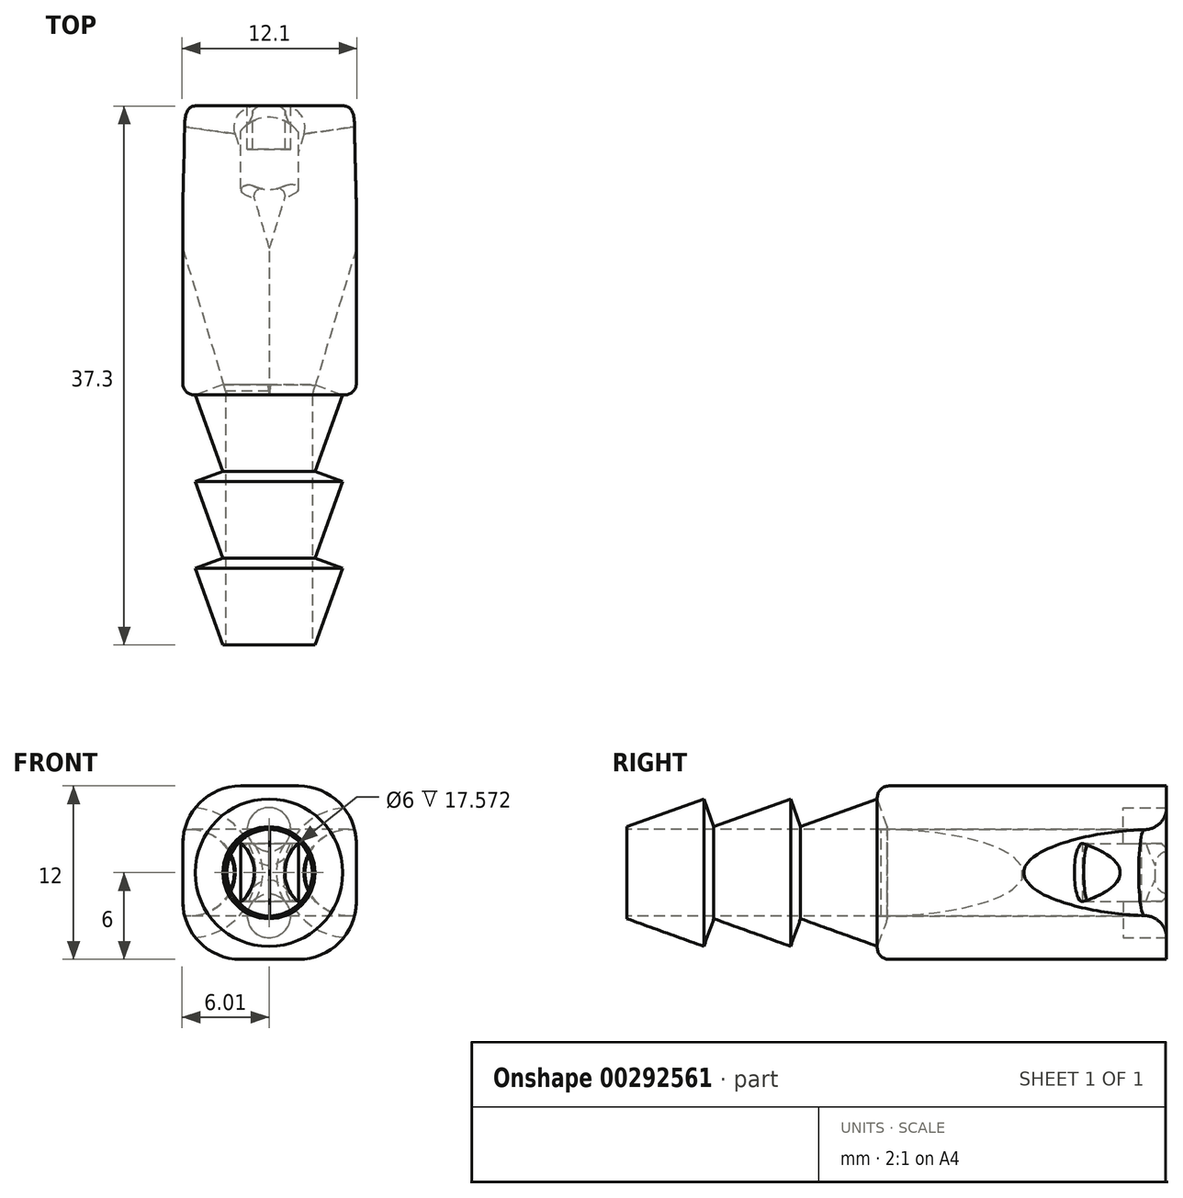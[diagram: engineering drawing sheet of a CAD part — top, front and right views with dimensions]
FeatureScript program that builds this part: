
annotation { "Feature Type Name" : "Feature", "Feature Type Description" : "" }
export const myFeature = defineFeature(function(context is Context, id is Id, definition is map)
    precondition{}
    {
        {
            var Q0;
            Q0=qCreatedBy(makeId("Right.planeOp"),FACE);
            var sketch = newSketch(context, id + "F0", { "sketchPlane" : qUnion([Q0])});
            skLineSegment(sketch, "E0", {"start": v(-28.57, 3.19) * mm, "end": v(-23.26, 5.1) * mm});
            skLineSegment(sketch, "E1", {"start": v(-23.26, 5.1) * mm, "end": v(-22.57, 3.19) * mm});
            skLineSegment(sketch, "E2", {"start": v(-22.57, 3.19) * mm, "end": v(-17.26, 5.1) * mm});
            skLineSegment(sketch, "E3", {"start": v(-17.26, 5.1) * mm, "end": v(-16.57, 3.19) * mm});
            skLineSegment(sketch, "E4", {"start": v(-16.57, 3.19) * mm, "end": v(-11.26, 5.1) * mm});
            skLineSegment(sketch, "E5", {"start": v(-11.26, 5.1) * mm, "end": v(-10.57, 3.19) * mm});
            skLineSegment(sketch, "E6", {"start": v(-10.57, 3.19) * mm, "end": v(-10.57, 0) * mm});
            skLineSegment(sketch, "E7", {"start": v(-28.57, 3.19) * mm, "end": v(-28.57, 0) * mm});
            skLineSegment(sketch, "E8", {"start": v(-28.57, 0) * mm, "end": v(-10.57, 0) * mm});
            skSolve(sketch);
        }
        {
            var Q0;
            Q0 = qSketchRegion(id + "F0", true);
            var Q1;
            Q1=sQuery(id+"F0.wireOp",EDGE,"E8");
            revolve(context, id + "F1", {"entities" : qUnion([Q0]), "axis" : qUnion([Q1]), "revolveType" : RevolveType.FULL});
        }
        {
            var Q0;
            Q0=makeQuery(id+"F1.opRevolve","SWEPT_FACE",FACE,{"disambiguationData":[OSD([sQuery(id+"F0.wireOp",EDGE,"E7")])]});
            var sketch = newSketch(context, id + "F2", { "sketchPlane" : qUnion([Q0])});
            skCircle(sketch, "E9", {"center": v(0, 0) * mm, "radius": 3 * mm});
            skSolve(sketch);
        }
        {
            var Q0;
            Q0=makeQuery(id+"F2.imprint","IMPRINT",FACE,{"disambiguationData":[TD([[makeQuery(id+"F2.imprint","IMPRINT",EDGE,{"derivedFrom":sQuery(id+"F2.wireOp",EDGE,"E9")}),1.0]])]});
            extrude(context, id + "F3", {"entities" : qUnion([Q0]), "operationType" : NewBodyOperationType.REMOVE, "oppositeDirection" : true, "depth" : 18.3 * mm});
        }
        {
            var Q0;
            Q0=qCreatedBy(makeId("Top.planeOp"),FACE);
            var sketch = newSketch(context, id + "F4", { "sketchPlane" : qUnion([Q0])});
            skLineSegment(sketch, "E10.bottom", {"start": v(-5.96, -11.27) * mm, "end": v(6.04, -11.27) * mm});
            skLineSegment(sketch, "E10.top", {"start": v(-5.96, 8.73) * mm, "end": v(6.04, 8.73) * mm});
            skLineSegment(sketch, "E10.left", {"start": v(-5.96, -11.27) * mm, "end": v(-5.96, 8.73) * mm});
            skLineSegment(sketch, "E10.right", {"start": v(6.04, -11.27) * mm, "end": v(6.04, 8.73) * mm});
            skSolve(sketch);
        }
        {
            var Q0;
            Q0 = qSketchRegion(id + "F4", true);
            extrude(context, id + "F5", {"entities" : qUnion([Q0]), "depth" : 6 * mm, "hasSecondDirection" : true, "secondDirectionOppositeDirection" : true, "secondDirectionDepth" : 6 * mm});
        }
        {
            var Q0;
            Q0=makeQuery(id+"F5.opExtrude","CAP_FACE",FACE,{"disambiguationData":[OSD([sQuery(id+"F4.wireOp",EDGE,"E10.bottom"),sQuery(id+"F4.wireOp",EDGE,"E10.top"),sQuery(id+"F4.wireOp",EDGE,"E10.left"),sQuery(id+"F4.wireOp",EDGE,"E10.right")])],"isStart":false});
            var sketch = newSketch(context, id + "F6", { "sketchPlane" : qUnion([Q0])});
            skLineSegment(sketch, "E11", {"start": v(6.04, 8.73) * mm, "end": v(0.04, -11.27) * mm});
            skLineSegment(sketch, "E12", {"start": v(6.04, 8.73) * mm, "end": v(16.48, 27.61) * mm});
            skLineSegment(sketch, "E13", {"start": v(16.48, 27.61) * mm, "end": v(-16.93, 27.61) * mm});
            skLineSegment(sketch, "E14", {"start": v(-16.93, 27.61) * mm, "end": v(-5.96, 8.73) * mm});
            skLineSegment(sketch, "E15", {"start": v(-5.96, 8.73) * mm, "end": v(0.04, -11.27) * mm});
            skSolve(sketch);
        }
        {
            var Q0;
            Q0=makeQuery(id+"F5.opExtrude","SWEPT_FACE",FACE,{"disambiguationData":[OSD([sQuery(id+"F4.wireOp",EDGE,"E10.bottom")])]});
            var sketch = newSketch(context, id + "F7", { "sketchPlane" : qUnion([Q0])});
            skCircle(sketch, "E16", {"center": v(0, 0) * mm, "radius": 3 * mm});
            skSolve(sketch);
        }
        {
            var Q0;
            Q0=makeQuery(id+"F7.imprint","IMPRINT",FACE,{"disambiguationData":[TD([[makeQuery(id+"F7.imprint","IMPRINT",EDGE,{"derivedFrom":sQuery(id+"F7.wireOp",EDGE,"E16")}),1.0]])]});
            var Q1;
            Q1=sQuery(id+"F6.wireOp",EDGE,"E11");
            var Q2;
            Q2=sQuery(id+"F6.wireOp",EDGE,"E12");
            var Q3;
            Q3=sQuery(id+"F6.wireOp",EDGE,"E13");
            var Q4;
            Q4=sQuery(id+"F6.wireOp",EDGE,"E14");
            var Q5;
            Q5=sQuery(id+"F6.wireOp",EDGE,"E15");
            sweep(context, id + "F8", {"operationType" : NewBodyOperationType.REMOVE, "profiles" : qUnion([Q0]), "path" : qUnion([Q1, Q2, Q3, Q4, Q5])});
        }
        {
            var Q0;
            Q0=makeQuery(id+"F5.opExtrude","CAP_EDGE",EDGE,{"disambiguationData":[OSD([sQuery(id+"F4.wireOp",EDGE,"E10.left")])],"isStart":true});
            var Q1;
            Q1=makeQuery(id+"F5.opExtrude","CAP_EDGE",EDGE,{"disambiguationData":[OSD([sQuery(id+"F4.wireOp",EDGE,"E10.left")])],"isStart":false});
            var Q2;
            Q2=makeQuery(id+"F5.opExtrude","CAP_EDGE",EDGE,{"disambiguationData":[OSD([sQuery(id+"F4.wireOp",EDGE,"E10.right")])],"isStart":false});
            var Q3;
            Q3=makeQuery(id+"F5.opExtrude","CAP_EDGE",EDGE,{"disambiguationData":[OSD([sQuery(id+"F4.wireOp",EDGE,"E10.right")])],"isStart":true});
            fillet(context, id + "F9", {"entities" : qUnion([Q0, Q1, Q2, Q3]), "radius" : 4 * mm, "tangentPropagation" : true, "allowEdgeOverflow" : false});
        }
        {
            var Q0;
            Q0=makeQuery(id+"F8.boolean.opBoolean","INTERSECT",EDGE,{"derivedFrom":[makeQuery(id+"F5.opExtrude","SWEPT_FACE",FACE,{"disambiguationData":[OSD([sQuery(id+"F4.wireOp",EDGE,"E10.top")])]}),makeQuery(id+"F8.opSweep","SWEPT_FACE",FACE,{"disambiguationData":[OSD([sQuery(id+"F6.wireOp",EDGE,"E15"),sQuery(id+"F7.wireOp",EDGE,"E16")])]})]});
            var Q1;
            Q1=makeQuery(id+"F8.boolean.opBoolean","INTERSECT",EDGE,{"derivedFrom":[makeQuery(id+"F5.opExtrude","SWEPT_FACE",FACE,{"disambiguationData":[OSD([sQuery(id+"F4.wireOp",EDGE,"E10.top")])]}),makeQuery(id+"F8.opSweep","SWEPT_FACE",FACE,{"disambiguationData":[OSD([sQuery(id+"F6.wireOp",EDGE,"E11"),sQuery(id+"F7.wireOp",EDGE,"E16")])]})]});
            fillet(context, id + "F10", {"entities" : qUnion([Q0, Q1]), "radius" : 1.5 * mm, "tangentPropagation" : true, "allowEdgeOverflow" : false});
        }
        {
            var Q0;
            Q0=makeQuery(id+"F9.opFillet","BLEND_EDGE",EDGE,{"blendedFrom":[makeQuery(id+"F5.opExtrude","CAP_EDGE",EDGE,{"disambiguationData":[OSD([sQuery(id+"F4.wireOp",EDGE,"E10.left")])],"isStart":false}),makeQuery(id+"F5.opExtrude","SWEPT_FACE",FACE,{"disambiguationData":[OSD([sQuery(id+"F4.wireOp",EDGE,"E10.bottom")])]})],"blendedInto":[makeQuery(id+"F5.opExtrude","SWEPT_FACE",FACE,{"disambiguationData":[OSD([sQuery(id+"F4.wireOp",EDGE,"E10.bottom")])]})]});
            fillet(context, id + "F11", {"entities" : qUnion([Q0]), "radius" : .8 * mm, "tangentPropagation" : true, "allowEdgeOverflow" : false});
        }
        {
            var Q0;
            Q0=makeQuery(id+"F5.opExtrude","CAP_FACE",FACE,{"disambiguationData":[OSD([sQuery(id+"F4.wireOp",EDGE,"E10.bottom"),sQuery(id+"F4.wireOp",EDGE,"E10.top"),sQuery(id+"F4.wireOp",EDGE,"E10.left"),sQuery(id+"F4.wireOp",EDGE,"E10.right")])],"isStart":false});
            var sketch = newSketch(context, id + "F12", { "sketchPlane" : qUnion([Q0])});
            skCircle(sketch, "E17", {"center": v(0, 5.45) * mm, "radius": 2.5 * mm});
            skSolve(sketch);
        }
        {
            var Q0;
            Q0=makeQuery(id+"F12.imprint","IMPRINT",FACE,{"disambiguationData":[TD([[makeQuery(id+"F12.imprint","IMPRINT",EDGE,{"derivedFrom":sQuery(id+"F12.wireOp",EDGE,"E17")}),1.0]])]});
            extrude(context, id + "F13", {"entities" : qUnion([Q0]), "operationType" : NewBodyOperationType.REMOVE, "oppositeDirection" : true, "depth" : 8 * mm, "hasSecondDirection" : true, "secondDirectionOppositeDirection" : true, "secondDirectionDepth" : 4 * mm});
        }
        {
            var Q0;
            {var subQ0=sQuery(id+"F12.wireOp",EDGE,"E17");var subQ1=sQuery(id+"F4.wireOp",EDGE,"E10.right");var subQ2=sQuery(id+"F4.wireOp",EDGE,"E10.left");var subQ3=makeQuery(id+"F5.opExtrude","CAP_FACE",FACE,{"disambiguationData":[OSD([sQuery(id+"F4.wireOp",EDGE,"E10.bottom"),sQuery(id+"F4.wireOp",EDGE,"E10.top"),subQ2,subQ1])],"isStart":false});Q0=makeQuery(id+"F13.boolean.opBoolean","INTERSECT",EDGE,{"derivedFrom":[makeQuery(id+"F8.boolean.opBoolean","COPY",FACE,{"derivedFrom":makeQuery(id+"F8.opSweep","SWEPT_FACE",FACE,{"disambiguationData":[OSD([sQuery(id+"F6.wireOp",EDGE,"E11"),sQuery(id+"F7.wireOp",EDGE,"E16")])]})}),makeQuery(id+"F13.opExtrude","SWEPT_FACE",FACE,{"disambiguationData":[OSD([subQ0]),TDD([makeQuery(id+"F12.imprint","IMPRINT",EDGE,{"disambiguationData":[TD([[makeQuery(id+"F12.imprint","INTERSECT",VERTEX,{"disambiguationData":[OD(1.0)],"derivedFrom":[makeQuery(id+"F9.opFillet","BLEND_EDGE",EDGE,{"blendedFrom":[makeQuery(id+"F5.opExtrude","CAP_EDGE",EDGE,{"disambiguationData":[OSD([subQ2])],"isStart":false}),subQ3],"blendedInto":[subQ3]}),subQ0]}),-1.0]])],"derivedFrom":subQ0})])]})]});}
            var Q1;
            {var subQ0=sQuery(id+"F12.wireOp",EDGE,"E17");var subQ1=sQuery(id+"F4.wireOp",EDGE,"E10.right");var subQ2=sQuery(id+"F4.wireOp",EDGE,"E10.left");var subQ3=makeQuery(id+"F5.opExtrude","CAP_FACE",FACE,{"disambiguationData":[OSD([sQuery(id+"F4.wireOp",EDGE,"E10.bottom"),sQuery(id+"F4.wireOp",EDGE,"E10.top"),subQ2,subQ1])],"isStart":false});Q1=makeQuery(id+"F13.boolean.opBoolean","INTERSECT",EDGE,{"derivedFrom":[makeQuery(id+"F8.boolean.opBoolean","COPY",FACE,{"derivedFrom":makeQuery(id+"F8.opSweep","SWEPT_FACE",FACE,{"disambiguationData":[OSD([sQuery(id+"F6.wireOp",EDGE,"E15"),sQuery(id+"F7.wireOp",EDGE,"E16")])]})}),makeQuery(id+"F13.opExtrude","SWEPT_FACE",FACE,{"disambiguationData":[OSD([subQ0]),TDD([makeQuery(id+"F12.imprint","IMPRINT",EDGE,{"disambiguationData":[TD([[makeQuery(id+"F12.imprint","INTERSECT",VERTEX,{"disambiguationData":[OD(1.0)],"derivedFrom":[makeQuery(id+"F9.opFillet","BLEND_EDGE",EDGE,{"blendedFrom":[makeQuery(id+"F5.opExtrude","CAP_EDGE",EDGE,{"disambiguationData":[OSD([subQ2])],"isStart":false}),subQ3],"blendedInto":[subQ3]}),subQ0]}),-1.0]])],"derivedFrom":subQ0})])]})]});}
            fillet(context, id + "F14", {"entities" : qUnion([Q0, Q1]), "radius" : .5 * mm, "tangentPropagation" : true, "allowEdgeOverflow" : false});
        }
        {
            var Q0;
            Q0=makeQuery(id+"F5.opExtrude","SWEPT_FACE",FACE,{"disambiguationData":[OSD([sQuery(id+"F4.wireOp",EDGE,"E10.top")])]});
            var sketch = newSketch(context, id + "F15", { "sketchPlane" : qUnion([Q0])});
            skCircle(sketch, "E18", {"center": v(0, 3) * mm, "radius": 1.5 * mm});
            skCircle(sketch, "E19", {"center": v(0, -3) * mm, "radius": 1.5 * mm});
            skSolve(sketch);
        }
        {
            var Q0;
            Q0 = qSketchRegion(id + "F15", true);
            extrude(context, id + "F16", {"entities" : qUnion([Q0]), "operationType" : NewBodyOperationType.REMOVE, "oppositeDirection" : true, "depth" : 3 * mm});
        }
        {
            var Q0;
            {var subQ0=sQuery(id+"F12.wireOp",EDGE,"E17");var subQ1=sQuery(id+"F4.wireOp",EDGE,"E10.right");var subQ2=sQuery(id+"F4.wireOp",EDGE,"E10.left");var subQ3=makeQuery(id+"F5.opExtrude","CAP_FACE",FACE,{"disambiguationData":[OSD([sQuery(id+"F4.wireOp",EDGE,"E10.bottom"),sQuery(id+"F4.wireOp",EDGE,"E10.top"),subQ2,subQ1])],"isStart":false});Q0=makeQuery(id+"F16.boolean.opBoolean","INTERSECT",EDGE,{"derivedFrom":[makeQuery(id+"F13.boolean.opBoolean","COPY",FACE,{"derivedFrom":makeQuery(id+"F13.opExtrude","SWEPT_FACE",FACE,{"disambiguationData":[OSD([subQ0]),TDD([makeQuery(id+"F12.imprint","IMPRINT",EDGE,{"disambiguationData":[TD([[makeQuery(id+"F12.imprint","INTERSECT",VERTEX,{"disambiguationData":[OD(0.0)],"derivedFrom":[makeQuery(id+"F9.opFillet","BLEND_EDGE",EDGE,{"blendedFrom":[makeQuery(id+"F5.opExtrude","CAP_EDGE",EDGE,{"disambiguationData":[OSD([subQ2])],"isStart":false}),subQ3],"blendedInto":[subQ3]}),subQ0]}),1.0]])],"derivedFrom":subQ0})])]})}),makeQuery(id+"F16.opExtrude","SWEPT_FACE",FACE,{"disambiguationData":[OSD([sQuery(id+"F15.wireOp",EDGE,"E18")])]})]});}
            var Q1;
            {var subQ0=sQuery(id+"F12.wireOp",EDGE,"E17");var subQ1=sQuery(id+"F4.wireOp",EDGE,"E10.right");var subQ2=sQuery(id+"F4.wireOp",EDGE,"E10.left");var subQ3=makeQuery(id+"F5.opExtrude","CAP_FACE",FACE,{"disambiguationData":[OSD([sQuery(id+"F4.wireOp",EDGE,"E10.bottom"),sQuery(id+"F4.wireOp",EDGE,"E10.top"),subQ2,subQ1])],"isStart":false});Q1=makeQuery(id+"F16.boolean.opBoolean","INTERSECT",EDGE,{"derivedFrom":[makeQuery(id+"F13.boolean.opBoolean","COPY",FACE,{"derivedFrom":makeQuery(id+"F13.opExtrude","SWEPT_FACE",FACE,{"disambiguationData":[OSD([subQ0]),TDD([makeQuery(id+"F12.imprint","IMPRINT",EDGE,{"disambiguationData":[TD([[makeQuery(id+"F12.imprint","INTERSECT",VERTEX,{"disambiguationData":[OD(0.0)],"derivedFrom":[makeQuery(id+"F9.opFillet","BLEND_EDGE",EDGE,{"blendedFrom":[makeQuery(id+"F5.opExtrude","CAP_EDGE",EDGE,{"disambiguationData":[OSD([subQ2])],"isStart":false}),subQ3],"blendedInto":[subQ3]}),subQ0]}),1.0]])],"derivedFrom":subQ0})])]})}),makeQuery(id+"F16.opExtrude","SWEPT_FACE",FACE,{"disambiguationData":[OSD([sQuery(id+"F15.wireOp",EDGE,"E19")])]})]});}
            fillet(context, id + "F17", {"entities" : qUnion([Q0, Q1]), "radius" : 1 * mm, "tangentPropagation" : true, "allowEdgeOverflow" : false});
        }
    });
